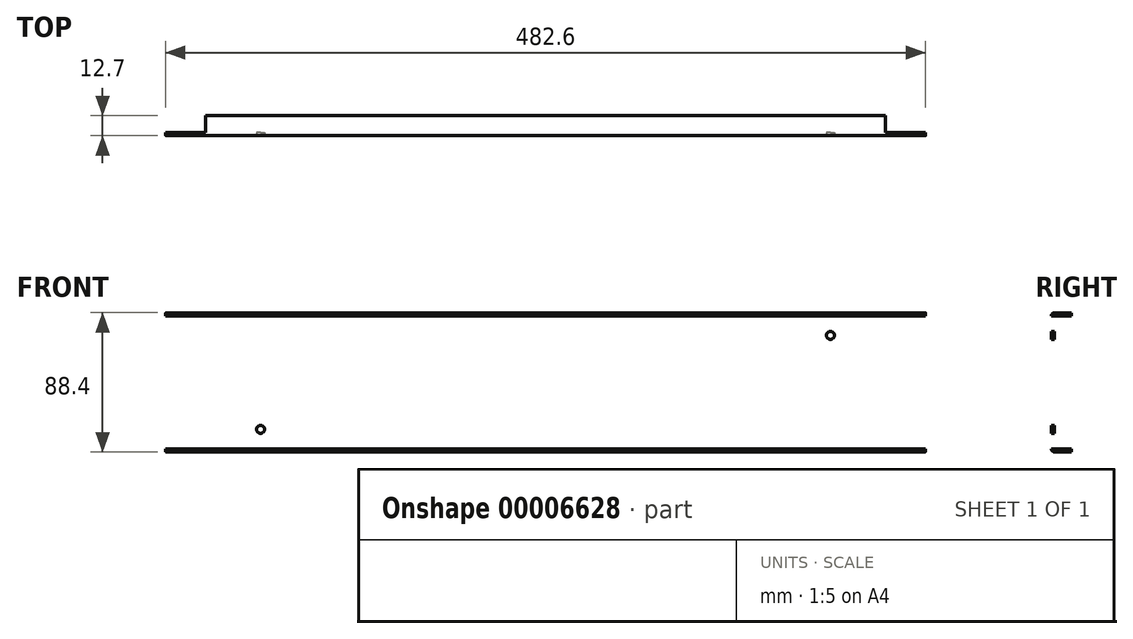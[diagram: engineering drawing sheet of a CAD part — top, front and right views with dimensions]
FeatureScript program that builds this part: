
annotation { "Feature Type Name" : "Feature", "Feature Type Description" : "" }
export const myFeature = defineFeature(function(context is Context, id is Id, definition is map)
    precondition{}
    {
        {
            var Q0;
            Q0=qCreatedBy(makeId("Right.planeOp"),FACE);
            var sketch = newSketch(context, id + "F0", { "sketchPlane" : qUnion([Q0])});
            skLineSegment(sketch, "E0", {"start": v(0, 42.16) * mm, "end": v(0, -42.16) * mm});
            skLineSegment(sketch, "E1", {"start": v(2.03, 44.2) * mm, "end": v(12.7, 44.2) * mm});
            skLineSegment(sketch, "E2", {"start": v(12.7, 44.2) * mm, "end": v(12.7, 42.16) * mm});
            skLineSegment(sketch, "E3", {"start": v(12.7, 42.16) * mm, "end": v(2.03, 42.16) * mm});
            skLineSegment(sketch, "E4", {"start": v(2.03, 42.16) * mm, "end": v(2.03, -42.16) * mm});
            skLineSegment(sketch, "E5", {"start": v(2.03, -42.16) * mm, "end": v(12.7, -42.16) * mm});
            skLineSegment(sketch, "E6", {"start": v(12.7, -42.16) * mm, "end": v(12.7, -44.2) * mm});
            skLineSegment(sketch, "E7", {"start": v(12.7, -44.2) * mm, "end": v(2.03, -44.2) * mm});
            skPoint(sketch, "E8.visualSharp", {"position": v(0, 44.2) * mm});
            skArc(sketch, "E8.filletArc", {"start": v(2.03, 44.2) * mm, "mid": v(0.6, 43.6) * mm, "end": v(0, 42.16) * mm});
            skPoint(sketch, "E9.visualSharp", {"position": v(0, -44.2) * mm});
            skArc(sketch, "E9.filletArc", {"start": v(0, -42.16) * mm, "mid": v(0.6, -43.6) * mm, "end": v(2.03, -44.2) * mm});
            skSolve(sketch);
        }
        {
            var Q0;
            Q0=makeQuery(id+"F0.imprint","IMPRINT",FACE,{"disambiguationData":[TD([[makeQuery(id+"F0.imprint","IMPRINT",EDGE,{"derivedFrom":sQuery(id+"F0.wireOp",EDGE,"E0")}),1.0]])]});
            extrude(context, id + "F1", {"entities" : qUnion([Q0]), "endBound" : BoundingType.SYMMETRIC, "depth" : 482.6 * mm});
        }
        {
            var Q0;
            Q0=makeQuery(id+"F1.opExtrude","SWEPT_FACE",FACE,{"disambiguationData":[OSD([sQuery(id+"F0.wireOp",EDGE,"E1")])]});
            var sketch = newSketch(context, id + "F2", { "sketchPlane" : qUnion([Q0])});
            skLineSegment(sketch, "E10", {"start": v(-241.3, 12.7) * mm, "end": v(-215.9, 12.7) * mm});
            skLineSegment(sketch, "E11", {"start": v(-215.9, 12.7) * mm, "end": v(-215.9, 2.03) * mm});
            skLineSegment(sketch, "E12", {"start": v(-215.9, 2.03) * mm, "end": v(-241.65, 2.03) * mm});
            skLineSegment(sketch, "E13", {"start": v(-241.65, 2.03) * mm, "end": v(-241.65, 12.7) * mm});
            skLineSegment(sketch, "E14", {"start": v(-241.65, 12.7) * mm, "end": v(-215.9, 12.7) * mm});
            skLineSegment(sketch, "E15", {"start": v(-212.95, 0) * mm, "end": v(-246.05, 0) * mm, "construction": true});
            skLineSegment(sketch, "E16.0.MirrorCS", {"start": v(241.65, 12.7) * mm, "end": v(215.9, 12.7) * mm});
            skLineSegment(sketch, "E16.1.MirrorCS", {"start": v(241.3, 12.7) * mm, "end": v(215.9, 12.7) * mm});
            skLineSegment(sketch, "E16.2.MirrorCS", {"start": v(215.9, 12.7) * mm, "end": v(215.9, 2.03) * mm});
            skLineSegment(sketch, "E16.3.MirrorCS", {"start": v(215.9, 2.03) * mm, "end": v(241.65, 2.03) * mm});
            skLineSegment(sketch, "E16.4.MirrorCS", {"start": v(241.65, 2.03) * mm, "end": v(241.65, 12.7) * mm});
            skSolve(sketch);
        }
        {
            var Q0;
            {var subQ7=sQuery(id+"F2.wireOp",EDGE,"E12");Q0=makeQuery(id+"F2.imprint","IMPRINT",FACE,{"disambiguationData":[TD([[makeQuery(id+"F2.imprint","IMPRINT",EDGE,{"derivedFrom":subQ7}),-1.0]])]});}
            var Q1;
            Q1=makeQuery(id+"F2.imprint","IMPRINT",FACE,{"disambiguationData":[TD([[makeQuery(id+"F2.imprint","IMPRINT",EDGE,{"derivedFrom":sQuery(id+"F2.wireOp",EDGE,"E16.0.MirrorCS")}),1.0]])]});
            var Q2;
            {var subQ0=sQuery(id+"F0.wireOp",EDGE,"E1");var subQ4=makeQuery(id+"F1.opExtrude","CAP_EDGE",EDGE,{"disambiguationData":[OSD([subQ0])],"isStart":true});Q2=makeQuery(id+"F2.imprint","IMPRINT",FACE,{"disambiguationData":[TD([[makeQuery(id+"F2.imprint","IMPRINT",EDGE,{"derivedFrom":subQ4}),-1.0]])]});}
            var Q3;
            {var subQ5=sQuery(id+"F2.wireOp",EDGE,"E16.1.MirrorCS");Q3=makeQuery(id+"F2.imprint","IMPRINT",FACE,{"disambiguationData":[TD([[makeQuery(id+"F2.imprint","IMPRINT",EDGE,{"derivedFrom":subQ5}),1.0]])]});}
            extrude(context, id + "F3", {"entities" : qUnion([Q0, Q1, Q2, Q3]), "operationType" : NewBodyOperationType.REMOVE, "oppositeDirection" : true, "depth" : 88.9 * mm});
        }
        {
            var Q0;
            Q0=makeQuery(id+"F1.opExtrude","SWEPT_FACE",FACE,{"disambiguationData":[OSD([sQuery(id+"F0.wireOp",EDGE,"E0")])]});
            var sketch = newSketch(context, id + "F4", { "sketchPlane" : qUnion([Q0])});
            skLineSegment(sketch, "E17", {"start": v(-234.47, 50.74) * mm, "end": v(-234.47, 14.93) * mm, "construction": true});
            skLineSegment(sketch, "E18", {"start": v(-230.4, 50.83) * mm, "end": v(-230.4, 16.37) * mm, "construction": true});
            skLineSegment(sketch, "E19", {"start": v(-241.26, 51.54) * mm, "end": v(-241.3, 31.15) * mm, "construction": true});
            skLineSegment(sketch, "E20", {"start": v(-255.4, 0) * mm, "end": v(-189.9, 0) * mm, "construction": true});
            skLineSegment(sketch, "E21", {"start": v(-252.21, 38.16) * mm, "end": v(-217.16, 38.16) * mm, "construction": true});
            skLineSegment(sketch, "E22", {"start": v(-235.23, 41.66) * mm, "end": v(-229.24, 41.66) * mm, "construction": true});
            skLineSegment(sketch, "E23", {"start": v(-235.59, 34.67) * mm, "end": v(-229.14, 34.67) * mm, "construction": true});
            skArc(sketch, "E24", {"start": v(-229.24, 41.66) * mm, "mid": v(-225.75, 38.21) * mm, "end": v(-229.14, 34.67) * mm});
            skArc(sketch, "E25", {"start": v(-235.23, 41.66) * mm, "mid": v(-238.72, 38.14) * mm, "end": v(-235.17, 34.67) * mm});
            skLineSegment(sketch, "E26", {"start": v(-235.23, 41.66) * mm, "end": v(-229.24, 41.66) * mm});
            skLineSegment(sketch, "E27", {"start": v(-229.14, 34.67) * mm, "end": v(-235.17, 34.67) * mm});
            skLineSegment(sketch, "E28.0.MirrorCS", {"start": v(-235.59, -34.67) * mm, "end": v(-229.14, -34.67) * mm, "construction": true});
            skLineSegment(sketch, "E28.1.MirrorCS", {"start": v(-235.23, -41.66) * mm, "end": v(-229.24, -41.66) * mm, "construction": true});
            skLineSegment(sketch, "E28.2.MirrorCS", {"start": v(-229.14, -34.67) * mm, "end": v(-235.17, -34.67) * mm});
            skArc(sketch, "E28.3.MirrorCS", {"start": v(-235.23, -41.66) * mm, "mid": v(-238.72, -38.14) * mm, "end": v(-235.17, -34.67) * mm});
            skLineSegment(sketch, "E28.4.MirrorCS", {"start": v(-235.23, -41.66) * mm, "end": v(-229.24, -41.66) * mm});
            skArc(sketch, "E28.5.MirrorCS", {"start": v(-229.24, -41.66) * mm, "mid": v(-225.75, -38.21) * mm, "end": v(-229.14, -34.67) * mm});
            skLineSegment(sketch, "E29.0.MirrorCS", {"start": v(235.23, -41.66) * mm, "end": v(229.24, -41.66) * mm, "construction": true});
            skLineSegment(sketch, "E29.1.MirrorCS", {"start": v(235.23, -41.66) * mm, "end": v(229.24, -41.66) * mm});
            skArc(sketch, "E29.2.MirrorCS", {"start": v(229.24, -41.66) * mm, "mid": v(225.75, -38.21) * mm, "end": v(229.14, -34.67) * mm});
            skLineSegment(sketch, "E29.3.MirrorCS", {"start": v(235.59, -34.67) * mm, "end": v(229.14, -34.67) * mm, "construction": true});
            skLineSegment(sketch, "E29.4.MirrorCS", {"start": v(229.14, -34.67) * mm, "end": v(235.17, -34.67) * mm});
            skArc(sketch, "E29.5.MirrorCS", {"start": v(235.23, -41.66) * mm, "mid": v(238.72, -38.14) * mm, "end": v(235.17, -34.67) * mm});
            skLineSegment(sketch, "E29.6.MirrorCS", {"start": v(235.23, 41.66) * mm, "end": v(229.24, 41.66) * mm, "construction": true});
            skLineSegment(sketch, "E29.7.MirrorCS", {"start": v(235.59, 34.67) * mm, "end": v(229.14, 34.67) * mm, "construction": true});
            skArc(sketch, "E29.8.MirrorCS", {"start": v(229.24, 41.66) * mm, "mid": v(225.75, 38.21) * mm, "end": v(229.14, 34.67) * mm});
            skArc(sketch, "E29.9.MirrorCS", {"start": v(235.23, 41.66) * mm, "mid": v(238.72, 38.14) * mm, "end": v(235.17, 34.67) * mm});
            skLineSegment(sketch, "E29.10.MirrorCS", {"start": v(229.14, 34.67) * mm, "end": v(235.17, 34.67) * mm});
            skLineSegment(sketch, "E29.11.MirrorCS", {"start": v(235.23, 41.66) * mm, "end": v(229.24, 41.66) * mm});
            skCircle(sketch, "E30", {"center": v(-180.98, 29.84) * mm, "radius": 2.54 * mm});
            skCircle(sketch, "E31.0.MirrorC", {"center": v(180.98, 29.84) * mm, "radius": 2.54 * mm});
            skCircle(sketch, "E32.0.MirrorC", {"center": v(-180.98, -29.84) * mm, "radius": 2.54 * mm});
            skCircle(sketch, "E33.0.MirrorC", {"center": v(180.98, -29.84) * mm, "radius": 2.54 * mm});
            skSolve(sketch);
        }
        {
            var Q0;
            {var subQ5=sQuery(id+"F4.wireOp",EDGE,"E27");Q0=makeQuery(id+"F4.imprint","IMPRINT",FACE,{"disambiguationData":[TD([[makeQuery(id+"F4.imprint","IMPRINT",EDGE,{"derivedFrom":subQ5}),-1.0]])]});}
            var Q1;
            {var subQ5=sQuery(id+"F4.wireOp",EDGE,"E28.2.MirrorCS");Q1=makeQuery(id+"F4.imprint","IMPRINT",FACE,{"disambiguationData":[TD([[makeQuery(id+"F4.imprint","IMPRINT",EDGE,{"derivedFrom":subQ5}),1.0]])]});}
            var Q2;
            {var subQ5=sQuery(id+"F4.wireOp",EDGE,"E29.10.MirrorCS");Q2=makeQuery(id+"F4.imprint","IMPRINT",FACE,{"disambiguationData":[TD([[makeQuery(id+"F4.imprint","IMPRINT",EDGE,{"derivedFrom":subQ5}),1.0]])]});}
            var Q3;
            {var subQ3=sQuery(id+"F4.wireOp",EDGE,"E29.4.MirrorCS");Q3=makeQuery(id+"F4.imprint","IMPRINT",FACE,{"disambiguationData":[TD([[makeQuery(id+"F4.imprint","IMPRINT",EDGE,{"derivedFrom":subQ3}),-1.0]])]});}
            var Q4;
            {var subQ5=sQuery(id+"F4.wireOp",EDGE,"E26");Q4=makeQuery(id+"F4.imprint","IMPRINT",FACE,{"disambiguationData":[TD([[makeQuery(id+"F4.imprint","IMPRINT",EDGE,{"derivedFrom":subQ5}),-1.0]])]});}
            var Q5;
            {var subQ5=sQuery(id+"F4.wireOp",EDGE,"E28.4.MirrorCS");Q5=makeQuery(id+"F4.imprint","IMPRINT",FACE,{"disambiguationData":[TD([[makeQuery(id+"F4.imprint","IMPRINT",EDGE,{"derivedFrom":subQ5}),1.0]])]});}
            var Q6;
            {var subQ5=sQuery(id+"F4.wireOp",EDGE,"E29.11.MirrorCS");Q6=makeQuery(id+"F4.imprint","IMPRINT",FACE,{"disambiguationData":[TD([[makeQuery(id+"F4.imprint","IMPRINT",EDGE,{"derivedFrom":subQ5}),1.0]])]});}
            var Q7;
            {var subQ5=sQuery(id+"F4.wireOp",EDGE,"E29.1.MirrorCS");Q7=makeQuery(id+"F4.imprint","IMPRINT",FACE,{"disambiguationData":[TD([[makeQuery(id+"F4.imprint","IMPRINT",EDGE,{"derivedFrom":subQ5}),-1.0]])]});}
            var Q8;
            Q8=makeQuery(id+"F4.imprint","IMPRINT",FACE,{"disambiguationData":[TD([[makeQuery(id+"F4.imprint","IMPRINT",EDGE,{"derivedFrom":sQuery(id+"F4.wireOp",EDGE,"E30")}),1.0]])]});
            var Q9;
            Q9=makeQuery(id+"F4.imprint","IMPRINT",FACE,{"disambiguationData":[TD([[makeQuery(id+"F4.imprint","IMPRINT",EDGE,{"derivedFrom":sQuery(id+"F4.wireOp",EDGE,"E32.0.MirrorC")}),-1.0]])]});
            var Q10;
            Q10=makeQuery(id+"F4.imprint","IMPRINT",FACE,{"disambiguationData":[TD([[makeQuery(id+"F4.imprint","IMPRINT",EDGE,{"derivedFrom":sQuery(id+"F4.wireOp",EDGE,"E31.0.MirrorC")}),-1.0]])]});
            var Q11;
            Q11=makeQuery(id+"F4.imprint","IMPRINT",FACE,{"disambiguationData":[TD([[makeQuery(id+"F4.imprint","IMPRINT",EDGE,{"derivedFrom":sQuery(id+"F4.wireOp",EDGE,"E33.0.MirrorC")}),1.0]])]});
            extrude(context, id + "F5", {"entities" : qUnion([Q0, Q1, Q2, Q3, Q4, Q5, Q6, Q7, Q8, Q9, Q10, Q11]), "operationType" : NewBodyOperationType.REMOVE, "oppositeDirection" : true, "depth" : 2.54 * mm});
        }
    });
